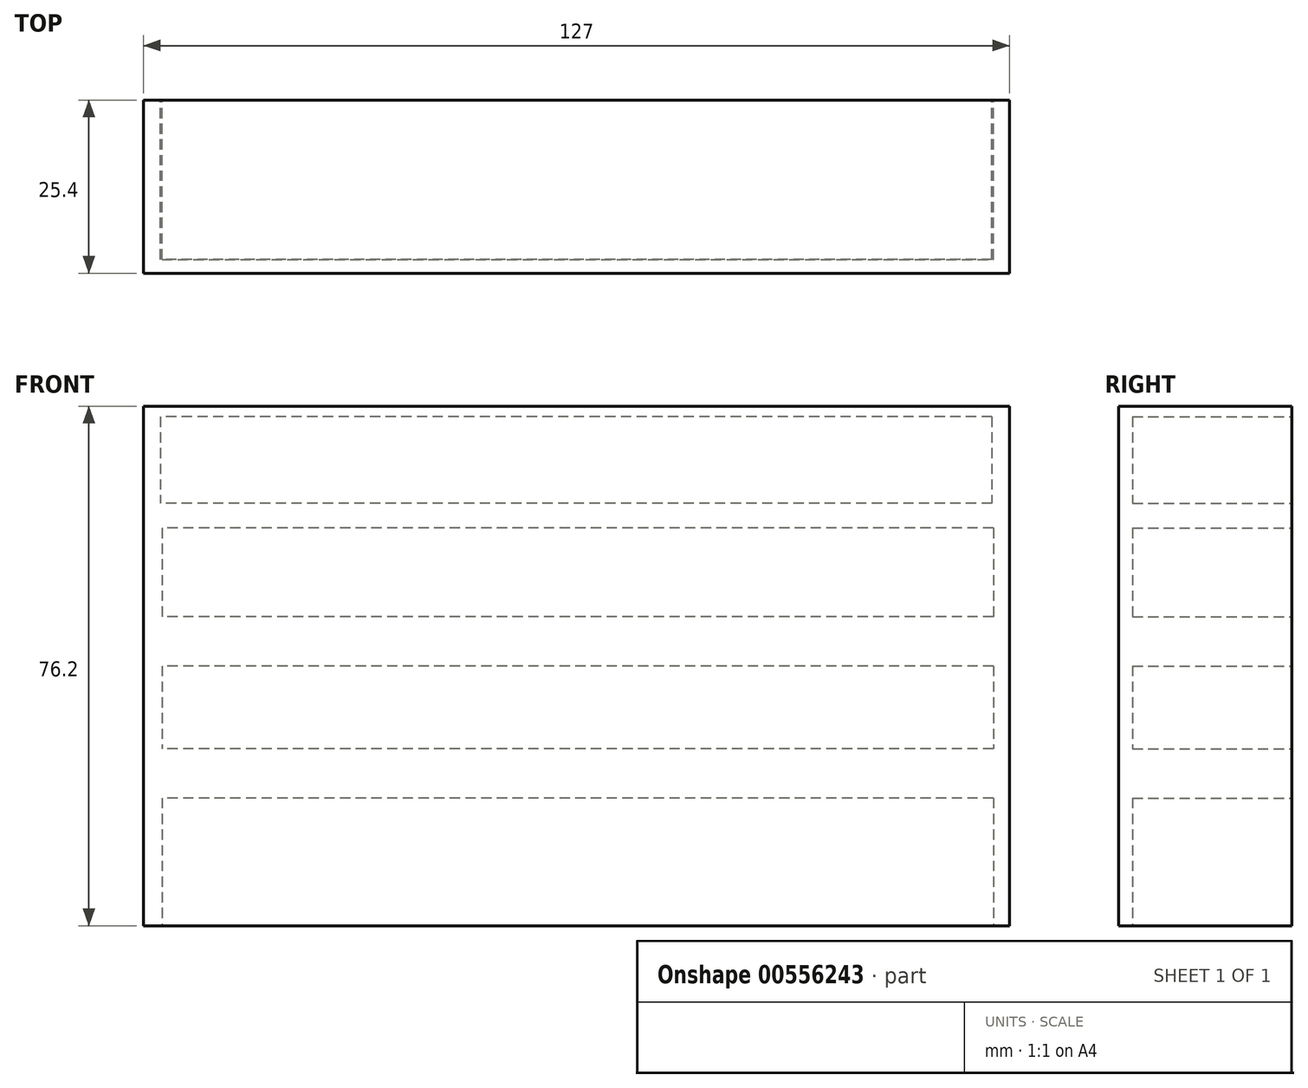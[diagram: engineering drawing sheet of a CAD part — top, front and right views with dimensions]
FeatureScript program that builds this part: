
annotation { "Feature Type Name" : "Feature", "Feature Type Description" : "" }
export const myFeature = defineFeature(function(context is Context, id is Id, definition is map)
    precondition{}
    {
        {
            var Q0;
            Q0=qCreatedBy(makeId("Top.planeOp"),FACE);
            var sketch = newSketch(context, id + "F0", { "sketchPlane" : qUnion([Q0])});
            skLineSegment(sketch, "E0.bottom", {"start": v(-84.62, 51.88) * mm, "end": v(42.38, 51.88) * mm});
            skLineSegment(sketch, "E0.top", {"start": v(-84.62, 26.48) * mm, "end": v(42.38, 26.48) * mm});
            skLineSegment(sketch, "E0.left", {"start": v(-84.62, 51.88) * mm, "end": v(-84.62, 26.48) * mm});
            skLineSegment(sketch, "E0.right", {"start": v(42.38, 51.88) * mm, "end": v(42.38, 26.48) * mm});
            skSolve(sketch);
        }
        {
            var Q0;
            Q0=makeQuery(id+"F0.imprint","IMPRINT",FACE,{"disambiguationData":[TD([[makeQuery(id+"F0.imprint","IMPRINT",EDGE,{"derivedFrom":sQuery(id+"F0.wireOp",EDGE,"E0.bottom")}),-1.0]])]});
            extrude(context, id + "F1", {"entities" : qUnion([Q0]), "depth" : 76.2 * mm, "offsetDistance" : 25.4 * mm});
        }
        {
            var Q0;
            Q0=makeQuery(id+"F1.opExtrude","SWEPT_FACE",FACE,{"disambiguationData":[OSD([sQuery(id+"F0.wireOp",EDGE,"E0.bottom")])]});
            var sketch = newSketch(context, id + "F2", { "sketchPlane" : qUnion([Q0])});
            skLineSegment(sketch, "E1.bottom", {"start": v(-39.8, 74.65) * mm, "end": v(82.13, 74.65) * mm});
            skLineSegment(sketch, "E1.top", {"start": v(-39.8, 61.95) * mm, "end": v(82.13, 61.95) * mm});
            skLineSegment(sketch, "E1.left", {"start": v(-39.8, 74.65) * mm, "end": v(-39.8, 61.95) * mm});
            skLineSegment(sketch, "E1.right", {"start": v(82.13, 74.65) * mm, "end": v(82.13, 61.95) * mm});
            skPoint(sketch, "E2.firstSnap0", {"position": v(-42.38, 38.1) * mm});
            skLineSegment(sketch, "E2.bottom", {"start": v(-40, 38.1) * mm, "end": v(81.92, 38.1) * mm});
            skLineSegment(sketch, "E2.top", {"start": v(-40, 25.96) * mm, "end": v(81.92, 25.96) * mm});
            skLineSegment(sketch, "E2.left", {"start": v(-40, 38.1) * mm, "end": v(-40, 25.96) * mm});
            skLineSegment(sketch, "E2.right", {"start": v(81.92, 38.1) * mm, "end": v(81.92, 25.96) * mm});
            skLineSegment(sketch, "E3.bottom", {"start": v(-40, 18.72) * mm, "end": v(81.92, 18.72) * mm});
            skLineSegment(sketch, "E3.top", {"start": v(-40, 0) * mm, "end": v(81.92, 0) * mm});
            skLineSegment(sketch, "E3.left", {"start": v(-40, 18.72) * mm, "end": v(-40, 0) * mm});
            skLineSegment(sketch, "E3.right", {"start": v(81.92, 18.72) * mm, "end": v(81.92, 0) * mm});
            skLineSegment(sketch, "E4.bottom", {"start": v(-40, 58.33) * mm, "end": v(81.92, 58.33) * mm});
            skLineSegment(sketch, "E4.top", {"start": v(-40, 45.34) * mm, "end": v(81.92, 45.34) * mm});
            skLineSegment(sketch, "E4.left", {"start": v(-40, 58.33) * mm, "end": v(-40, 45.34) * mm});
            skLineSegment(sketch, "E4.right", {"start": v(81.92, 58.33) * mm, "end": v(81.92, 45.34) * mm});
            skSolve(sketch);
        }
        {
            var Q0;
            Q0=makeQuery(id+"F2.imprint","IMPRINT",FACE,{"disambiguationData":[TD([[makeQuery(id+"F2.imprint","IMPRINT",EDGE,{"derivedFrom":sQuery(id+"F2.wireOp",EDGE,"E1.bottom")}),-1.0]])]});
            var Q1;
            Q1=makeQuery(id+"F2.imprint","IMPRINT",FACE,{"disambiguationData":[TD([[makeQuery(id+"F2.imprint","IMPRINT",EDGE,{"derivedFrom":sQuery(id+"F2.wireOp",EDGE,"E4.bottom")}),-1.0]])]});
            var Q2;
            Q2=makeQuery(id+"F2.imprint","IMPRINT",FACE,{"disambiguationData":[TD([[makeQuery(id+"F2.imprint","IMPRINT",EDGE,{"derivedFrom":sQuery(id+"F2.wireOp",EDGE,"E2.bottom")}),-1.0]])]});
            var Q3;
            Q3=makeQuery(id+"F2.imprint","IMPRINT",FACE,{"disambiguationData":[TD([[makeQuery(id+"F2.imprint","IMPRINT",EDGE,{"derivedFrom":sQuery(id+"F2.wireOp",EDGE,"E3.bottom")}),-1.0]])]});
            extrude(context, id + "F3", {"entities" : qUnion([Q0, Q1, Q2, Q3]), "operationType" : NewBodyOperationType.REMOVE, "oppositeDirection" : true, "depth" : 23.37 * mm, "offsetDistance" : 25.4 * mm});
        }
    });
